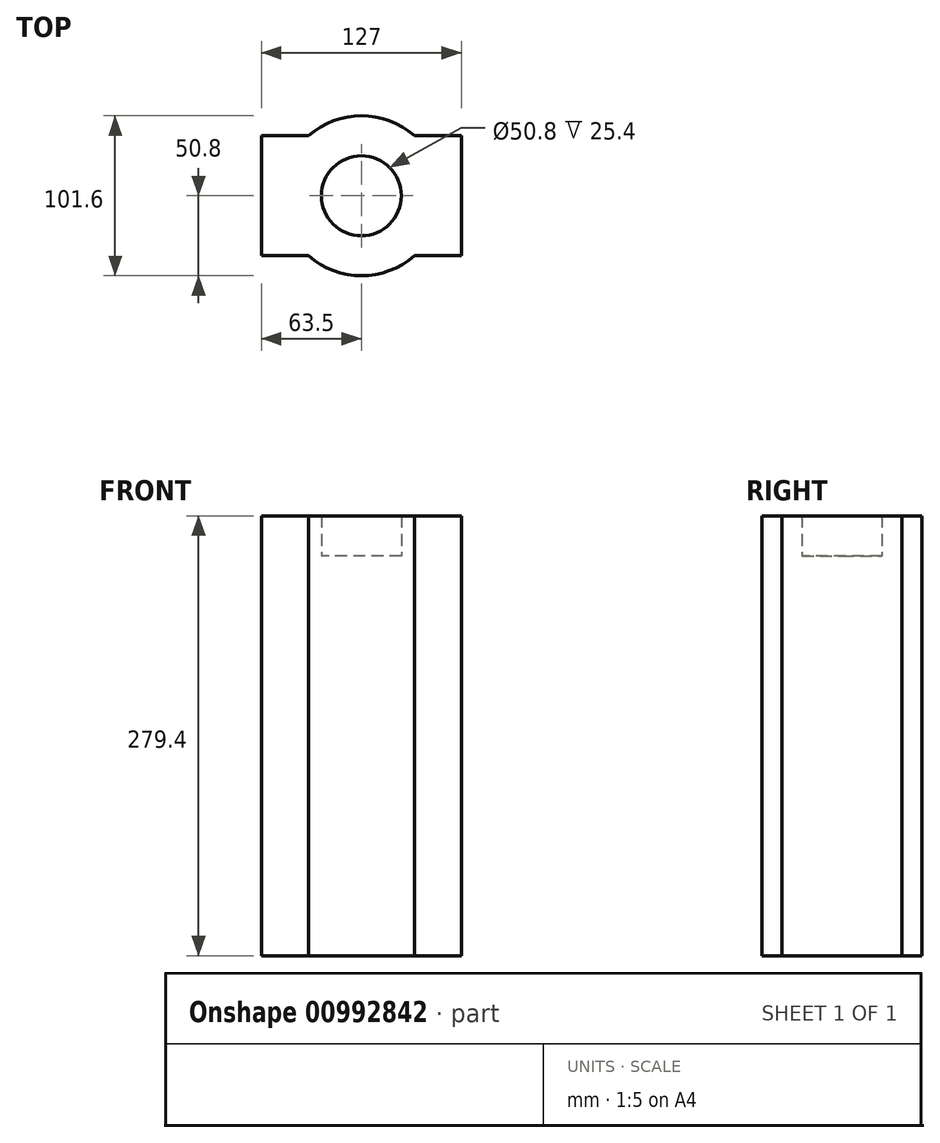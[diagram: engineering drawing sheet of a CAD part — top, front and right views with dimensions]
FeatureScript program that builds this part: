
annotation { "Feature Type Name" : "Feature", "Feature Type Description" : "" }
export const myFeature = defineFeature(function(context is Context, id is Id, definition is map)
    precondition{}
    {
        {
            var Q0;
            Q0=qCreatedBy(makeId("Top.planeOp"),FACE);
            var sketch = newSketch(context, id + "F0", { "sketchPlane" : qUnion([Q0])});
            skArc(sketch, "E0", {"start": v(-33.6, -38.1) * mm, "mid": v(0, -50.8) * mm, "end": v(33.6, -38.1) * mm});
            skLineSegment(sketch, "E1.bottom", {"start": v(63.5, 38.1) * mm, "end": v(33.6, 38.1) * mm});
            skLineSegment(sketch, "E1.top", {"start": v(63.5, -38.1) * mm, "end": v(33.6, -38.1) * mm});
            skLineSegment(sketch, "E1.left", {"start": v(63.5, 38.1) * mm, "end": v(63.5, -38.1) * mm});
            skLineSegment(sketch, "E1.right", {"start": v(-63.5, 38.1) * mm, "end": v(-63.5, -38.1) * mm});
            skLineSegment(sketch, "E2.trimOffspring", {"start": v(-33.6, 38.1) * mm, "end": v(-63.5, 38.1) * mm});
            skLineSegment(sketch, "E3.trimOffspring", {"start": v(-33.6, -38.1) * mm, "end": v(-63.5, -38.1) * mm});
            skArc(sketch, "E4.trimOffspring", {"start": v(33.6, 38.1) * mm, "mid": v(0, 50.8) * mm, "end": v(-33.6, 38.1) * mm});
            skSolve(sketch);
        }
        {
            var Q0;
            Q0 = qSketchRegion(id + "F0", true);
            extrude(context, id + "F1", {"entities" : qUnion([Q0]), "depth" : 254 * mm, "offsetDistance" : 25.4 * mm});
        }
        {
            var Q0;
            Q0=makeQuery(id+"F1.opExtrude","CAP_FACE",FACE,{"disambiguationData":[OSD([sQuery(id+"F0.wireOp",EDGE,"E0"),sQuery(id+"F0.wireOp",EDGE,"E1.bottom"),sQuery(id+"F0.wireOp",EDGE,"E1.top"),sQuery(id+"F0.wireOp",EDGE,"E1.left"),sQuery(id+"F0.wireOp",EDGE,"E1.right"),sQuery(id+"F0.wireOp",EDGE,"E2.trimOffspring"),sQuery(id+"F0.wireOp",EDGE,"E3.trimOffspring"),sQuery(id+"F0.wireOp",EDGE,"E4.trimOffspring")])],"isStart":false});
            var sketch = newSketch(context, id + "F2", { "sketchPlane" : qUnion([Q0])});
            skCircle(sketch, "E5", {"center": v(0, 0) * mm, "radius": 25.4 * mm});
            skSolve(sketch);
        }
        {
            var Q0;
            Q0=makeQuery(id+"F2.imprint","IMPRINT",FACE,{"disambiguationData":[TD([[makeQuery(id+"F2.imprint","IMPRINT",EDGE,{"derivedFrom":sQuery(id+"F2.wireOp",EDGE,"E5")}),-1.0]])]});
            extrude(context, id + "F3", {"entities" : qUnion([Q0]), "operationType" : NewBodyOperationType.ADD, "depth" : 25.4 * mm, "offsetDistance" : 25.4 * mm});
        }
    });
